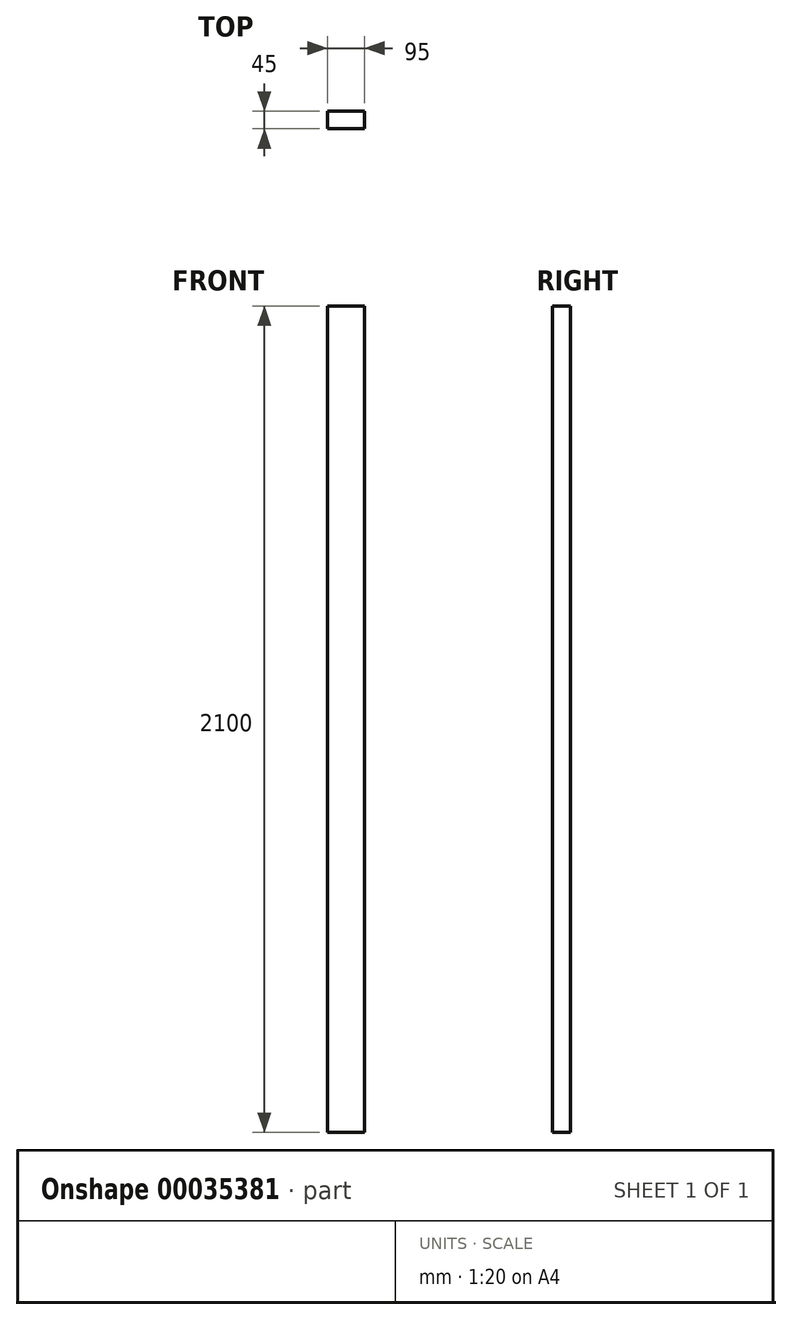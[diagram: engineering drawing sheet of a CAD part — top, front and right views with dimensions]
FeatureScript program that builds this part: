
annotation { "Feature Type Name" : "Feature", "Feature Type Description" : "" }
export const myFeature = defineFeature(function(context is Context, id is Id, definition is map)
    precondition{}
    {
        {
            var Q0;
            Q0=qCreatedBy(makeId("Top.planeOp"),FACE);
            var sketch = newSketch(context, id + "F0", { "sketchPlane" : qUnion([Q0])});
            skLineSegment(sketch, "E0.rect.bottom", {"start": v(47.5, -22.5) * mm, "end": v(-47.5, -22.5) * mm});
            skLineSegment(sketch, "E0.rect.top", {"start": v(47.5, 22.5) * mm, "end": v(-47.5, 22.5) * mm});
            skLineSegment(sketch, "E0.rect.left", {"start": v(47.5, -22.5) * mm, "end": v(47.5, 22.5) * mm});
            skLineSegment(sketch, "E0.rect.right", {"start": v(-47.5, -22.5) * mm, "end": v(-47.5, 22.5) * mm});
            skPoint(sketch, "E0.rect.middle", {"position": v(0, 0) * mm});
            skSolve(sketch);
        }
        {
            var Q0;
            Q0=makeQuery(id+"F0.imprint","IMPRINT",FACE,{"disambiguationData":[TD([[makeQuery(id+"F0.imprint","IMPRINT",EDGE,{"derivedFrom":sQuery(id+"F0.wireOp",EDGE,"E0.rect.bottom")}),-1.0]])]});
            extrude(context, id + "F1", {"entities" : qUnion([Q0]), "depth" : 2100 * mm});
        }
    });
